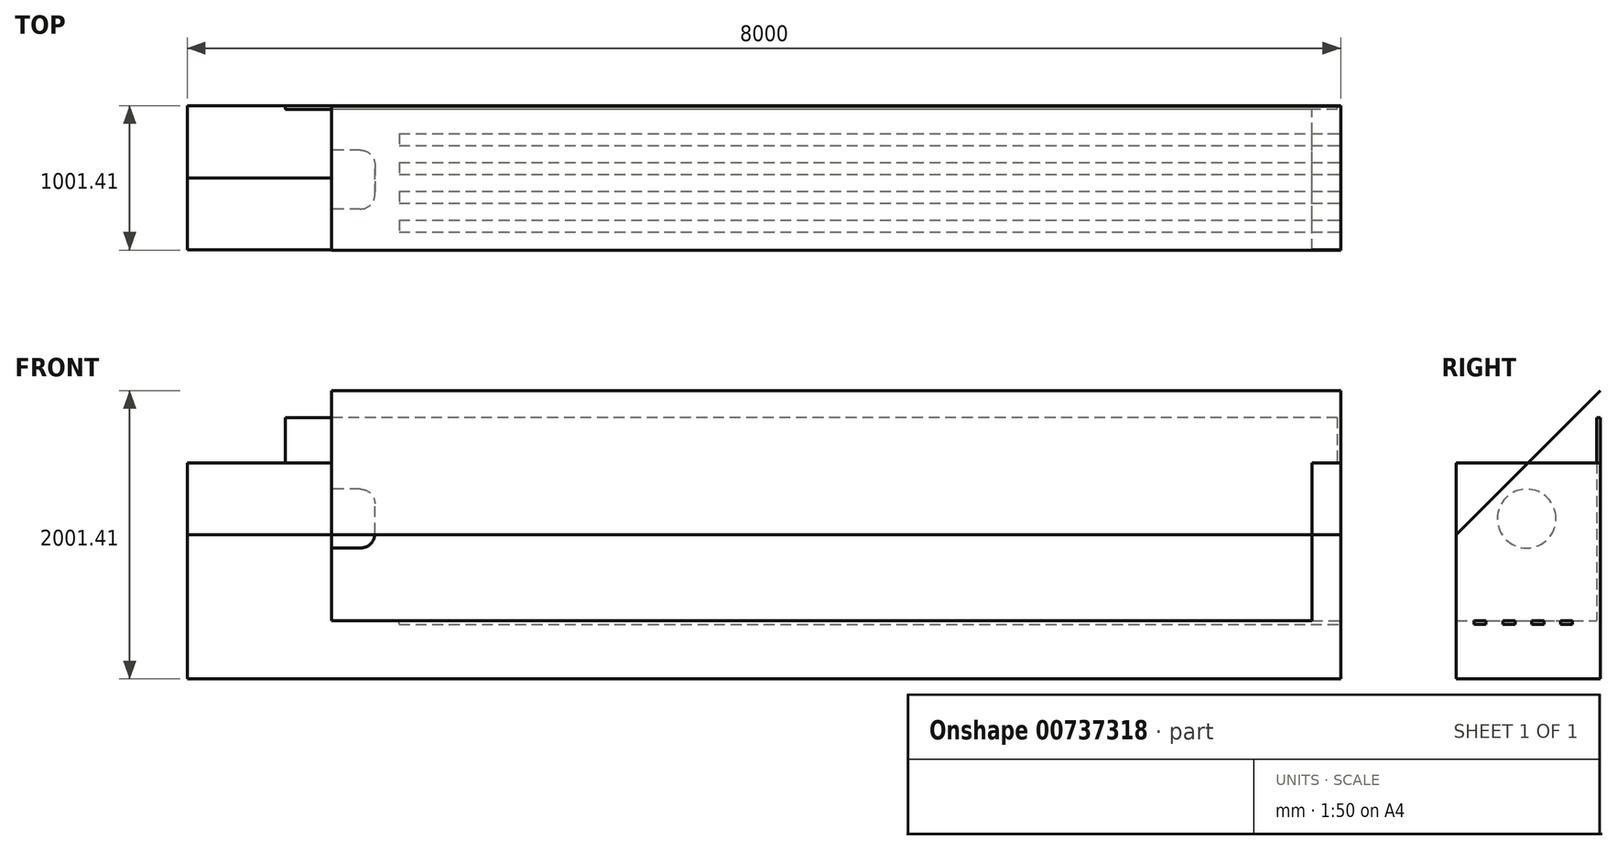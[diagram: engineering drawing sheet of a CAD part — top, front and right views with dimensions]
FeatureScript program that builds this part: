
annotation { "Feature Type Name" : "Feature", "Feature Type Description" : "" }
export const myFeature = defineFeature(function(context is Context, id is Id, definition is map)
    precondition{}
    {
        {
            var Q0;
            Q0=qCreatedBy(makeId("Front.planeOp"),FACE);
            var sketch = newSketch(context, id + "F0", { "sketchPlane" : qUnion([Q0])});
            skLineSegment(sketch, "E0", {"start": v(-2871.36, 1500) * mm, "end": v(-1871.36, 1500) * mm});
            skLineSegment(sketch, "E1", {"start": v(-1871.36, 1500) * mm, "end": v(-1871.36, 402.07) * mm});
            skLineSegment(sketch, "E2", {"start": v(-1871.36, 402.07) * mm, "end": v(4928.64, 402.07) * mm});
            skLineSegment(sketch, "E3", {"start": v(4928.64, 402.07) * mm, "end": v(4928.64, 1500) * mm});
            skLineSegment(sketch, "E4", {"start": v(4928.64, 1500) * mm, "end": v(5128.64, 1500) * mm});
            skLineSegment(sketch, "E5", {"start": v(5128.64, 1500) * mm, "end": v(5128.64, 0) * mm});
            skLineSegment(sketch, "E6", {"start": v(5128.64, 0) * mm, "end": v(-2871.36, 0) * mm});
            skLineSegment(sketch, "E7", {"start": v(-2871.36, 0) * mm, "end": v(-2871.36, 1500) * mm});
            skSolve(sketch);
        }
        {
            var Q0;
            Q0 = qSketchRegion(id + "F0", true);
            extrude(context, id + "F1", {"entities" : qUnion([Q0]), "depth" : 1000 * mm, "offsetDistance" : 25 * mm});
        }
        {
            var Q0;
            Q0=makeQuery(id+"F1.opExtrude","CAP_FACE",FACE,{"disambiguationData":[OSD([sQuery(id+"F0.wireOp",EDGE,"E0"),sQuery(id+"F0.wireOp",EDGE,"E1"),sQuery(id+"F0.wireOp",EDGE,"E2"),sQuery(id+"F0.wireOp",EDGE,"E3"),sQuery(id+"F0.wireOp",EDGE,"E4"),sQuery(id+"F0.wireOp",EDGE,"E5"),sQuery(id+"F0.wireOp",EDGE,"E6"),sQuery(id+"F0.wireOp",EDGE,"E7")])],"isStart":true});
            var sketch = newSketch(context, id + "F2", { "sketchPlane" : qUnion([Q0])});
            skLineSegment(sketch, "E8.bottom", {"start": v(-5105.1, 1813.26) * mm, "end": v(2192.15, 1813.26) * mm});
            skLineSegment(sketch, "E8.top", {"start": v(-5105.1, 240.56) * mm, "end": v(2192.15, 240.56) * mm});
            skLineSegment(sketch, "E8.left", {"start": v(-5105.1, 1813.26) * mm, "end": v(-5105.1, 240.56) * mm});
            skLineSegment(sketch, "E8.right", {"start": v(2192.15, 1813.26) * mm, "end": v(2192.15, 240.56) * mm});
            skSolve(sketch);
        }
        {
            var Q0;
            Q0 = qSketchRegion(id + "F2", true);
            extrude(context, id + "F3", {"entities" : qUnion([Q0]), "operationType" : NewBodyOperationType.ADD, "oppositeDirection" : true, "depth" : 25 * mm, "offsetDistance" : 25 * mm});
        }
        {
            var Q0;
            Q0=makeQuery(id+"F1.opExtrude","SWEPT_FACE",FACE,{"disambiguationData":[OSD([sQuery(id+"F0.wireOp",EDGE,"E1")])]});
            var sketch = newSketch(context, id + "F4", { "sketchPlane" : qUnion([Q0])});
            skCircle(sketch, "E9", {"center": v(-511.82, 1111.94) * mm, "radius": 204.27 * mm});
            skSolve(sketch);
        }
        {
            var Q0;
            Q0 = qSketchRegion(id + "F4", true);
            extrude(context, id + "F5", {"entities" : qUnion([Q0]), "operationType" : NewBodyOperationType.ADD, "depth" : 300 * mm, "offsetDistance" : 25 * mm});
        }
        {
            var Q0;
            Q0=makeQuery(id+"F1.opExtrude","CAP_EDGE",EDGE,{"disambiguationData":[OSD([sQuery(id+"F0.wireOp",EDGE,"E0")])],"isStart":false});
            chamfer(context, id + "F6", {"entities" : qUnion([Q0]), "width" : 500 * mm, "tangentPropagation" : true});
        }
        {
            var Q0;
            Q0=makeQuery(id+"F5.opExtrude","CAP_EDGE",EDGE,{"disambiguationData":[OSD([sQuery(id+"F4.wireOp",EDGE,"E9")])],"isStart":false});
            fillet(context, id + "F7", {"entities" : qUnion([Q0]), "radius" : 100 * mm, "tangentPropagation" : true, "allowEdgeOverflow" : false});
        }
        {
            var Q0;
            Q0=makeQuery(id+"F1.opExtrude","SWEPT_FACE",FACE,{"disambiguationData":[OSD([sQuery(id+"F0.wireOp",EDGE,"E2")])]});
            var sketch = newSketch(context, id + "F8", { "sketchPlane" : qUnion([Q0])});
            skLineSegment(sketch, "E10.bottom", {"start": v(-1402.97, -192.8) * mm, "end": v(5748.48, -192.8) * mm});
            skLineSegment(sketch, "E10.top", {"start": v(-1402.97, -275.83) * mm, "end": v(5748.48, -275.83) * mm});
            skLineSegment(sketch, "E10.left", {"start": v(-1402.97, -192.8) * mm, "end": v(-1402.97, -275.83) * mm});
            skLineSegment(sketch, "E10.right", {"start": v(5748.48, -192.8) * mm, "end": v(5748.48, -275.83) * mm});
            skLineSegment(sketch, "E11.0.1.0", {"start": v(-1402.97, -392.8) * mm, "end": v(5748.48, -392.8) * mm});
            skLineSegment(sketch, "E11.0.1.1", {"start": v(-1402.97, -475.83) * mm, "end": v(5748.48, -475.83) * mm});
            skLineSegment(sketch, "E11.0.1.2", {"start": v(-1402.97, -392.8) * mm, "end": v(-1402.97, -475.83) * mm});
            skLineSegment(sketch, "E11.0.1.3", {"start": v(5748.48, -392.8) * mm, "end": v(5748.48, -475.83) * mm});
            skLineSegment(sketch, "E11.0.2.0", {"start": v(-1402.97, -592.8) * mm, "end": v(5748.48, -592.8) * mm});
            skLineSegment(sketch, "E11.0.2.1", {"start": v(-1402.97, -675.83) * mm, "end": v(5748.48, -675.83) * mm});
            skLineSegment(sketch, "E11.0.2.2", {"start": v(-1402.97, -592.8) * mm, "end": v(-1402.97, -675.83) * mm});
            skLineSegment(sketch, "E11.0.2.3", {"start": v(5748.48, -592.8) * mm, "end": v(5748.48, -675.83) * mm});
            skLineSegment(sketch, "E11.direction1", {"start": v(-1402.97, -275.83) * mm, "end": v(-1202.97, -275.83) * mm, "construction": true});
            skLineSegment(sketch, "E11.direction2", {"start": v(-1402.97, -275.83) * mm, "end": v(-1402.97, -475.83) * mm, "construction": true});
            skLineSegment(sketch, "E12.0.0.3", {"start": v(-1402.97, -792.8) * mm, "end": v(5748.48, -792.8) * mm});
            skLineSegment(sketch, "E12.3.0.3", {"start": v(-1402.97, -875.83) * mm, "end": v(5748.48, -875.83) * mm});
            skLineSegment(sketch, "E12.6.0.3", {"start": v(-1402.97, -792.8) * mm, "end": v(-1402.97, -875.83) * mm});
            skLineSegment(sketch, "E12.9.0.3", {"start": v(5748.48, -792.8) * mm, "end": v(5748.48, -875.83) * mm});
            skSolve(sketch);
        }
        {
            var Q0;
            Q0 = qSketchRegion(id + "F8", true);
            extrude(context, id + "F9", {"entities" : qUnion([Q0]), "operationType" : NewBodyOperationType.REMOVE, "oppositeDirection" : true, "depth" : 25 * mm, "offsetDistance" : 25 * mm});
        }
        {
            var Q0;
            Q0=makeQuery(id+"F6.opChamfer","BLEND_FACE",FACE,{"disambiguationData":[OSD([sQuery(id+"F0.wireOp",EDGE,"E0")])]});
            var sketch = newSketch(context, id + "F10", { "sketchPlane" : qUnion([Q0])});
            skLineSegment(sketch, "E13.bottom", {"start": v(-1871.36, 1414.21) * mm, "end": v(5128.64, 1414.21) * mm});
            skLineSegment(sketch, "E13.top", {"start": v(-1871.36, 0) * mm, "end": v(5128.64, 0) * mm});
            skLineSegment(sketch, "E13.left", {"start": v(-1871.36, 1414.21) * mm, "end": v(-1871.36, 0) * mm});
            skLineSegment(sketch, "E13.right", {"start": v(5128.64, 1414.21) * mm, "end": v(5128.64, 0) * mm});
            skSolve(sketch);
        }
        {
            var Q0;
            Q0 = qSketchRegion(id + "F10", true);
            extrude(context, id + "F11", {"entities" : qUnion([Q0]), "depth" : 2 * mm, "offsetDistance" : 25 * mm});
        }
    });
